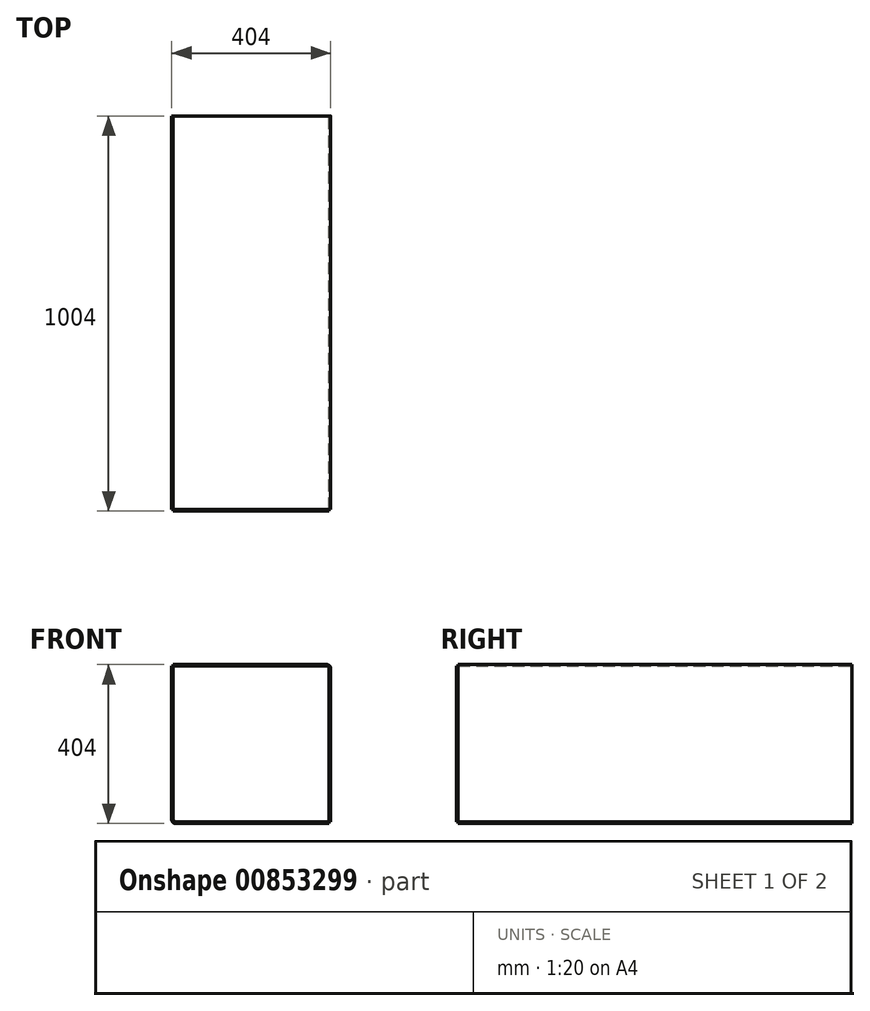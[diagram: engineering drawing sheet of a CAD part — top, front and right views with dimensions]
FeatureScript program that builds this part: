
annotation { "Feature Type Name" : "Feature", "Feature Type Description" : "" }
export const myFeature = defineFeature(function(context is Context, id is Id, definition is map)
    precondition{}
    {
        {
            var Q0;
            Q0=qCreatedBy(makeId("Front.planeOp"),FACE);
            var sketch = newSketch(context, id + "F0", { "sketchPlane" : qUnion([Q0])});
            skLineSegment(sketch, "E0", {"start": v(-196, 200) * mm, "end": v(194, 200) * mm});
            skLineSegment(sketch, "E1", {"start": v(200, 194) * mm, "end": v(200, -196) * mm});
            skLineSegment(sketch, "E2", {"start": v(200, -196) * mm, "end": v(204, -196) * mm});
            skLineSegment(sketch, "E3", {"start": v(204, -196) * mm, "end": v(204, 194) * mm});
            skLineSegment(sketch, "E4", {"start": v(194, 204) * mm, "end": v(-196, 204) * mm});
            skLineSegment(sketch, "E5", {"start": v(-196, 204) * mm, "end": v(-196, 200) * mm});
            skPoint(sketch, "E6.visualSharp", {"position": v(200, 200) * mm});
            skArc(sketch, "E6.filletArc", {"start": v(200, 194) * mm, "mid": v(198.24, 198.24) * mm, "end": v(194, 200) * mm});
            skPoint(sketch, "E7.visualSharp", {"position": v(204, 204) * mm});
            skArc(sketch, "E7.filletArc", {"start": v(204, 194) * mm, "mid": v(201.07, 201.07) * mm, "end": v(194, 204) * mm});
            skLineSegment(sketch, "E8", {"start": v(-196, 200) * mm, "end": v(-196, -190) * mm});
            skLineSegment(sketch, "E9", {"start": v(-190, -196) * mm, "end": v(200, -196) * mm});
            skLineSegment(sketch, "E10", {"start": v(200, -196) * mm, "end": v(200, -200) * mm});
            skLineSegment(sketch, "E11", {"start": v(200, -200) * mm, "end": v(-190, -200) * mm});
            skLineSegment(sketch, "E12", {"start": v(-200, -190) * mm, "end": v(-200, 200) * mm});
            skLineSegment(sketch, "E13", {"start": v(-200, 200) * mm, "end": v(-196, 200) * mm});
            skPoint(sketch, "E14.visualSharp", {"position": v(-196, -196) * mm});
            skArc(sketch, "E14.filletArc", {"start": v(-196, -190) * mm, "mid": v(-194.24, -194.24) * mm, "end": v(-190, -196) * mm});
            skPoint(sketch, "E15.visualSharp", {"position": v(-200, -200) * mm});
            skArc(sketch, "E15.filletArc", {"start": v(-200, -190) * mm, "mid": v(-197.07, -197.07) * mm, "end": v(-190, -200) * mm});
            skSolve(sketch);
        }
        {
            var Q0;
            Q0=makeQuery(id+"F0.imprint","IMPRINT",FACE,{"disambiguationData":[TD([[makeQuery(id+"F0.imprint","IMPRINT",EDGE,{"derivedFrom":sQuery(id+"F0.wireOp",EDGE,"E0")}),1.0]])]});
            extrude(context, id + "F1", {"entities" : qUnion([Q0]), "endBound" : BoundingType.SYMMETRIC, "depth" : 1000 * mm, "offsetDistance" : 25 * mm});
        }
        {
            var Q0;
            Q0=makeQuery(id+"F0.imprint","IMPRINT",FACE,{"disambiguationData":[TD([[makeQuery(id+"F0.imprint","IMPRINT",EDGE,{"derivedFrom":sQuery(id+"F0.wireOp",EDGE,"E8")}),-1.0]])]});
            extrude(context, id + "F2", {"entities" : qUnion([Q0]), "endBound" : BoundingType.SYMMETRIC, "depth" : 1000 * mm, "offsetDistance" : 25 * mm});
        }
        {
            var Q0;
            Q0=makeQuery(id+"F0.imprint","IMPRINT",FACE,{"disambiguationData":[TD([[makeQuery(id+"F0.imprint","IMPRINT",EDGE,{"derivedFrom":sQuery(id+"F0.wireOp",EDGE,"E0")}),-1.0]])]});
            extrude(context, id + "F3", {"entities" : qUnion([Q0]), "depth" : 504 * mm, "offsetDistance" : 25 * mm, "hasSecondDirection" : true, "secondDirectionOppositeDirection" : false, "secondDirectionDepth" : 500 * mm});
        }
    });
